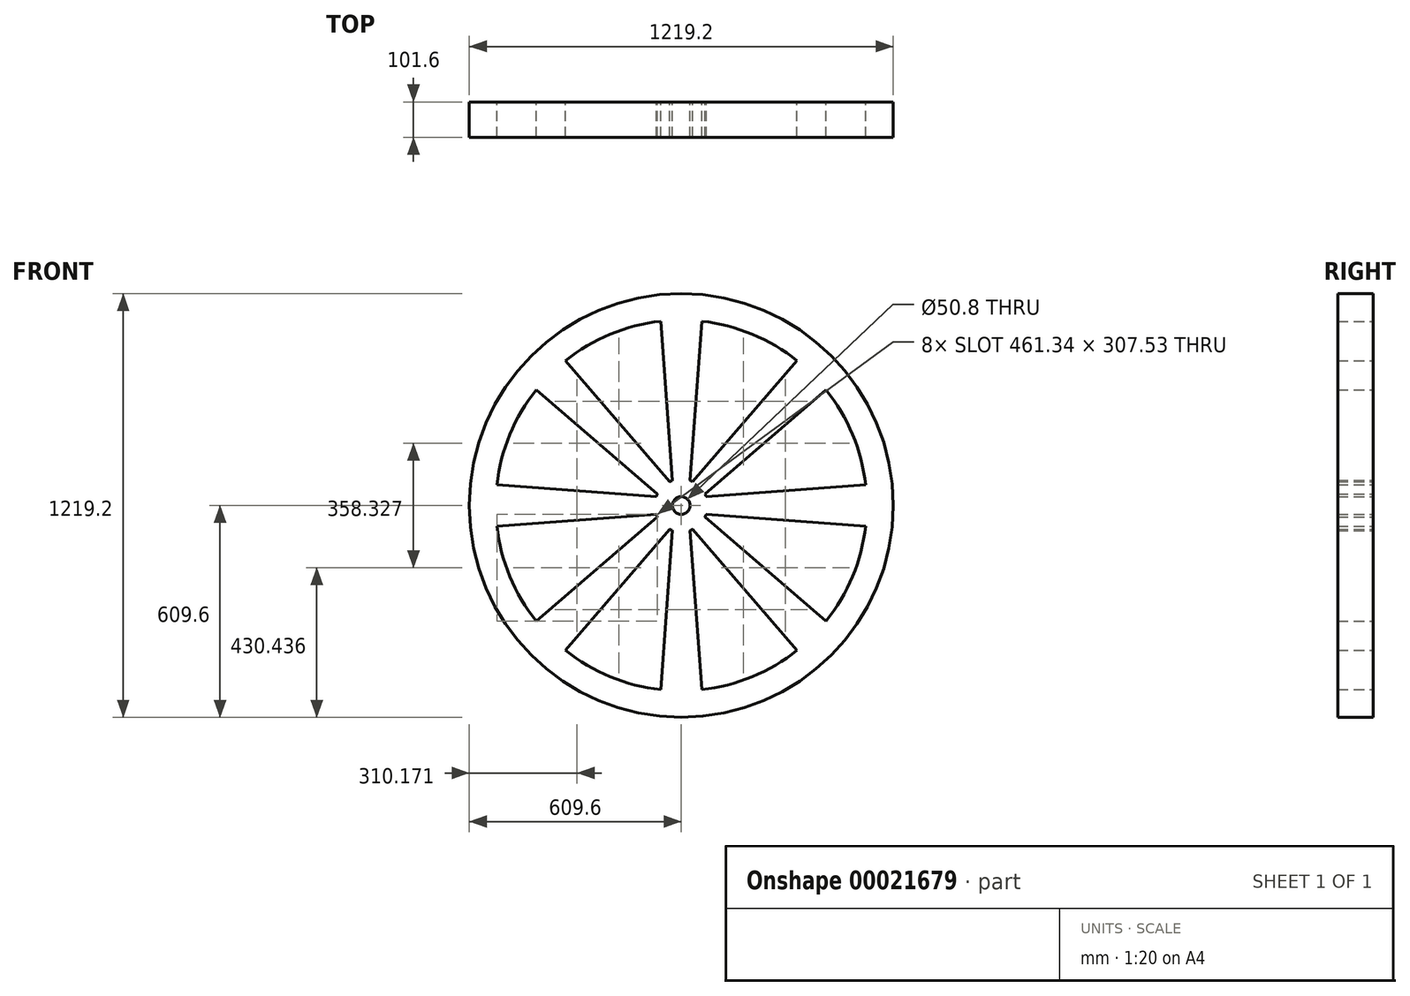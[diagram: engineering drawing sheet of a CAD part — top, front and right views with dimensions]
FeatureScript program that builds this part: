
annotation { "Feature Type Name" : "Feature", "Feature Type Description" : "" }
export const myFeature = defineFeature(function(context is Context, id is Id, definition is map)
    precondition{}
    {
        {
            var Q0;
            Q0=qCreatedBy(makeId("Front.planeOp"),FACE);
            var sketch = newSketch(context, id + "F0", { "sketchPlane" : qUnion([Q0])});
            skCircle(sketch, "E0", {"center": v(0, 0) * mm, "radius": 609.6 * mm});
            skArc(sketch, "E1.0", {"start": v(-59.27, 530.1) * mm, "mid": v(-204.12, 492.8) * mm, "end": v(-332.93, 416.74) * mm});
            skArc(sketch, "E2", {"start": v(-25.4, 71.84) * mm, "mid": v(-29.16, 70.4) * mm, "end": v(-32.84, 68.76) * mm});
            skCircle(sketch, "E3", {"center": v(0, 0) * mm, "radius": 25.4 * mm});
            skLineSegment(sketch, "E4.0", {"start": v(25.4, 71.84) * mm, "end": v(59.27, 530.1) * mm});
            skLineSegment(sketch, "E5.0", {"start": v(-25.4, 71.84) * mm, "end": v(-59.27, 530.1) * mm});
            skLineSegment(sketch, "E6.trimOffspring", {"start": v(-64.89, 606.14) * mm, "end": v(-64.99, 607.5) * mm});
            skPoint(sketch, "E7.start.orphan", {"position": v(0, 14.72) * mm});
            skLineSegment(sketch, "E8.1.0", {"start": v(-68.76, 32.84) * mm, "end": v(-416.74, 332.93) * mm});
            skLineSegment(sketch, "E8.1.1", {"start": v(-32.84, 68.76) * mm, "end": v(-332.93, 416.74) * mm});
            skLineSegment(sketch, "E8.2.0", {"start": v(-71.84, -25.4) * mm, "end": v(-530.1, -59.27) * mm});
            skLineSegment(sketch, "E8.2.1", {"start": v(-71.84, 25.4) * mm, "end": v(-530.1, 59.27) * mm});
            skLineSegment(sketch, "E8.3.0", {"start": v(-32.84, -68.76) * mm, "end": v(-332.93, -416.74) * mm});
            skLineSegment(sketch, "E8.3.1", {"start": v(-68.76, -32.84) * mm, "end": v(-416.74, -332.93) * mm});
            skLineSegment(sketch, "E8.4.0", {"start": v(25.4, -71.84) * mm, "end": v(59.27, -530.1) * mm});
            skLineSegment(sketch, "E8.4.1", {"start": v(-25.4, -71.84) * mm, "end": v(-59.27, -530.1) * mm});
            skLineSegment(sketch, "E8.5.0", {"start": v(68.76, -32.84) * mm, "end": v(416.74, -332.93) * mm});
            skLineSegment(sketch, "E8.5.1", {"start": v(32.84, -68.76) * mm, "end": v(332.93, -416.74) * mm});
            skLineSegment(sketch, "E8.6.0", {"start": v(71.84, 25.4) * mm, "end": v(530.1, 59.27) * mm});
            skLineSegment(sketch, "E8.6.1", {"start": v(71.84, -25.4) * mm, "end": v(530.1, -59.27) * mm});
            skLineSegment(sketch, "E8.7.0", {"start": v(32.84, 68.76) * mm, "end": v(332.93, 416.74) * mm});
            skLineSegment(sketch, "E8.7.1", {"start": v(68.76, 32.84) * mm, "end": v(416.74, 332.93) * mm});
            skArc(sketch, "E9.trimOffspring", {"start": v(-68.76, 32.84) * mm, "mid": v(-70.4, 29.16) * mm, "end": v(-71.84, 25.4) * mm});
            skArc(sketch, "E10.trimOffspring", {"start": v(-416.74, 332.93) * mm, "mid": v(-492.8, 204.12) * mm, "end": v(-530.1, 59.27) * mm});
            skArc(sketch, "E11.trimOffspring", {"start": v(-530.1, -59.27) * mm, "mid": v(-492.8, -204.12) * mm, "end": v(-416.74, -332.93) * mm});
            skArc(sketch, "E12.trimOffspring", {"start": v(-332.93, -416.74) * mm, "mid": v(-204.12, -492.8) * mm, "end": v(-59.27, -530.1) * mm});
            skArc(sketch, "E13.trimOffspring", {"start": v(-71.84, -25.4) * mm, "mid": v(-70.4, -29.16) * mm, "end": v(-68.76, -32.84) * mm});
            skArc(sketch, "E14.trimOffspring", {"start": v(-32.84, -68.76) * mm, "mid": v(-29.16, -70.4) * mm, "end": v(-25.4, -71.84) * mm});
            skArc(sketch, "E15.trimOffspring", {"start": v(25.4, -71.84) * mm, "mid": v(29.16, -70.4) * mm, "end": v(32.84, -68.76) * mm});
            skArc(sketch, "E16.trimOffspring", {"start": v(59.27, -530.1) * mm, "mid": v(204.12, -492.8) * mm, "end": v(332.93, -416.74) * mm});
            skArc(sketch, "E17.trimOffspring", {"start": v(416.74, -332.93) * mm, "mid": v(492.8, -204.12) * mm, "end": v(530.1, -59.27) * mm});
            skArc(sketch, "E18.trimOffspring", {"start": v(68.76, -32.84) * mm, "mid": v(70.4, -29.16) * mm, "end": v(71.84, -25.4) * mm});
            skArc(sketch, "E19.trimOffspring", {"start": v(71.84, 25.4) * mm, "mid": v(70.4, 29.16) * mm, "end": v(68.76, 32.84) * mm});
            skArc(sketch, "E20.trimOffspring", {"start": v(530.1, 59.27) * mm, "mid": v(492.8, 204.12) * mm, "end": v(416.74, 332.93) * mm});
            skArc(sketch, "E21.trimOffspring", {"start": v(332.93, 416.74) * mm, "mid": v(204.12, 492.8) * mm, "end": v(59.27, 530.1) * mm});
            skArc(sketch, "E22.trimOffspring", {"start": v(32.84, 68.76) * mm, "mid": v(29.16, 70.4) * mm, "end": v(25.4, 71.84) * mm});
            skSolve(sketch);
        }
        {
            var Q0;
            Q0=makeQuery(id+"F0.imprint","IMPRINT",FACE,{"disambiguationData":[TD([[makeQuery(id+"F0.imprint","IMPRINT",EDGE,{"derivedFrom":sQuery(id+"F0.wireOp",EDGE,"E0")}),1.0]])]});
            extrude(context, id + "F1", {"entities" : qUnion([Q0]), "depth" : 101.6 * mm});
        }
    });
